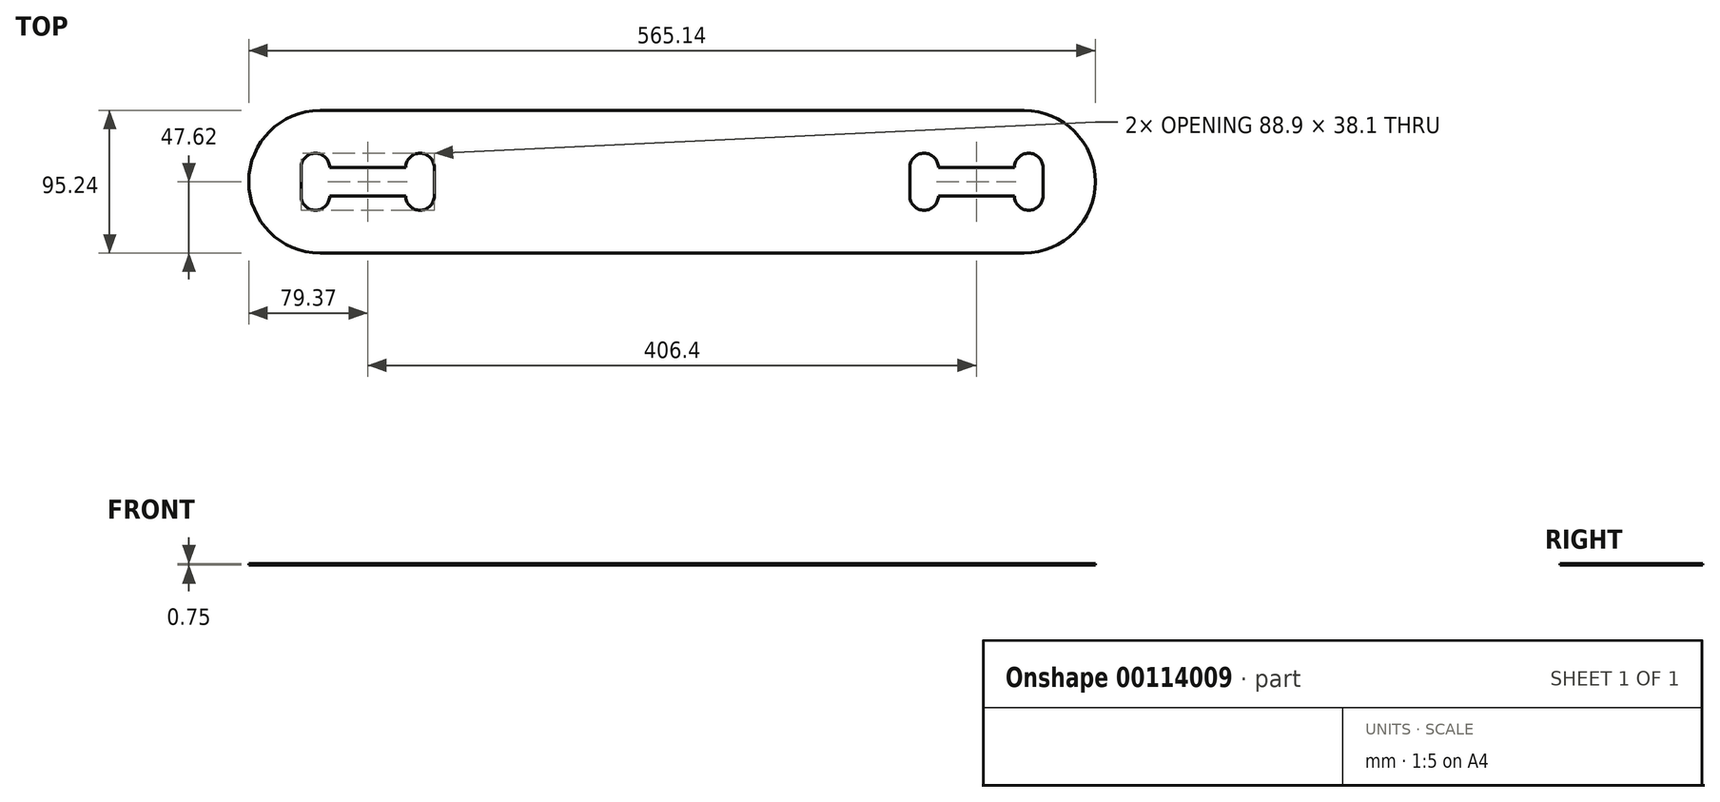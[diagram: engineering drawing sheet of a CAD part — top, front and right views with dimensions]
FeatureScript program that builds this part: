
annotation { "Feature Type Name" : "Feature", "Feature Type Description" : "" }
export const myFeature = defineFeature(function(context is Context, id is Id, definition is map)
    precondition{}
    {
        {
            assignVariable(context, id + "F0", {"name" : "thickness", "anyValue" : 0.75});
        }
        {
            var Q0;
            Q0=qCreatedBy(makeId("Top.planeOp"),FACE);
            var sketch = newSketch(context, id + "F1", { "sketchPlane" : qUnion([Q0])});
            skLineSegment(sketch, "E0.bottom", {"start": v(-234.95, 47.63) * mm, "end": v(234.95, 47.63) * mm});
            skLineSegment(sketch, "E0.top", {"start": v(-234.95, -47.63) * mm, "end": v(234.95, -47.63) * mm});
            skLineSegment(sketch, "E0.left", {"start": v(-234.95, 47.63) * mm, "end": v(-234.95, -47.63) * mm});
            skLineSegment(sketch, "E0.right", {"start": v(234.95, 47.62) * mm, "end": v(234.95, -47.62) * mm});
            skLineSegment(sketch, "E1", {"start": v(0, 47.62) * mm, "end": v(0, -47.63) * mm, "construction": true});
            skPoint(sketch, "E2", {"position": v(0, 0) * mm});
            skArc(sketch, "E3", {"start": v(-234.95, 47.63) * mm, "mid": v(-282.58, 0) * mm, "end": v(-234.95, -47.62) * mm});
            skArc(sketch, "E4", {"start": v(234.95, -47.63) * mm, "mid": v(282.58, 0) * mm, "end": v(234.95, 47.63) * mm});
            skLineSegment(sketch, "E5.bottom", {"start": v(-247.65, 9.52) * mm, "end": v(-158.75, 9.52) * mm});
            skLineSegment(sketch, "E5.top", {"start": v(-247.65, -9.52) * mm, "end": v(-158.75, -9.52) * mm});
            skLineSegment(sketch, "E5.left", {"start": v(-247.65, 9.52) * mm, "end": v(-247.65, -9.52) * mm});
            skLineSegment(sketch, "E5.right", {"start": v(-158.75, 9.52) * mm, "end": v(-158.75, -9.52) * mm});
            skLineSegment(sketch, "E6", {"start": v(-247.65, 0) * mm, "end": v(-158.75, 0) * mm, "construction": true});
            skArc(sketch, "E7", {"start": v(-228.6, 9.53) * mm, "mid": v(-238.13, 19.05) * mm, "end": v(-247.65, 9.52) * mm});
            skLineSegment(sketch, "E8", {"start": v(-203.2, 9.52) * mm, "end": v(-203.2, -9.52) * mm, "construction": true});
            skArc(sketch, "E9.MirrorCS", {"start": v(-177.8, 9.52) * mm, "mid": v(-168.27, 19.05) * mm, "end": v(-158.75, 9.52) * mm});
            skArc(sketch, "E10.MirrorCS", {"start": v(-177.8, -9.52) * mm, "mid": v(-168.27, -19.05) * mm, "end": v(-158.75, -9.52) * mm});
            skArc(sketch, "E11.MirrorCS", {"start": v(-228.6, -9.52) * mm, "mid": v(-238.13, -19.05) * mm, "end": v(-247.65, -9.52) * mm});
            skArc(sketch, "E12.MirrorCS", {"start": v(228.6, -9.53) * mm, "mid": v(238.13, -19.05) * mm, "end": v(247.65, -9.53) * mm});
            skLineSegment(sketch, "E13.MirrorCS", {"start": v(247.65, -9.52) * mm, "end": v(158.75, -9.52) * mm});
            skArc(sketch, "E14.MirrorCS", {"start": v(177.8, -9.53) * mm, "mid": v(168.27, -19.05) * mm, "end": v(158.75, -9.52) * mm});
            skLineSegment(sketch, "E15.MirrorCS", {"start": v(158.75, 9.52) * mm, "end": v(158.75, -9.52) * mm});
            skLineSegment(sketch, "E16.MirrorCS", {"start": v(247.65, 9.53) * mm, "end": v(158.75, 9.53) * mm});
            skLineSegment(sketch, "E17.MirrorCS", {"start": v(247.65, 9.52) * mm, "end": v(247.65, -9.53) * mm});
            skArc(sketch, "E18.MirrorCS", {"start": v(228.6, 9.53) * mm, "mid": v(238.13, 19.05) * mm, "end": v(247.65, 9.52) * mm});
            skArc(sketch, "E19.MirrorCS", {"start": v(177.8, 9.53) * mm, "mid": v(168.27, 19.05) * mm, "end": v(158.75, 9.52) * mm});
            skSolve(sketch);
        }
        {
            var Q0;
            Q0 = qSketchRegion(id + "F1", true);
            extrude(context, id + "F2", {"entities" : qUnion([Q0]), "depth" : (getVariable(context, 'thickness')) * mm});
        }
    });
